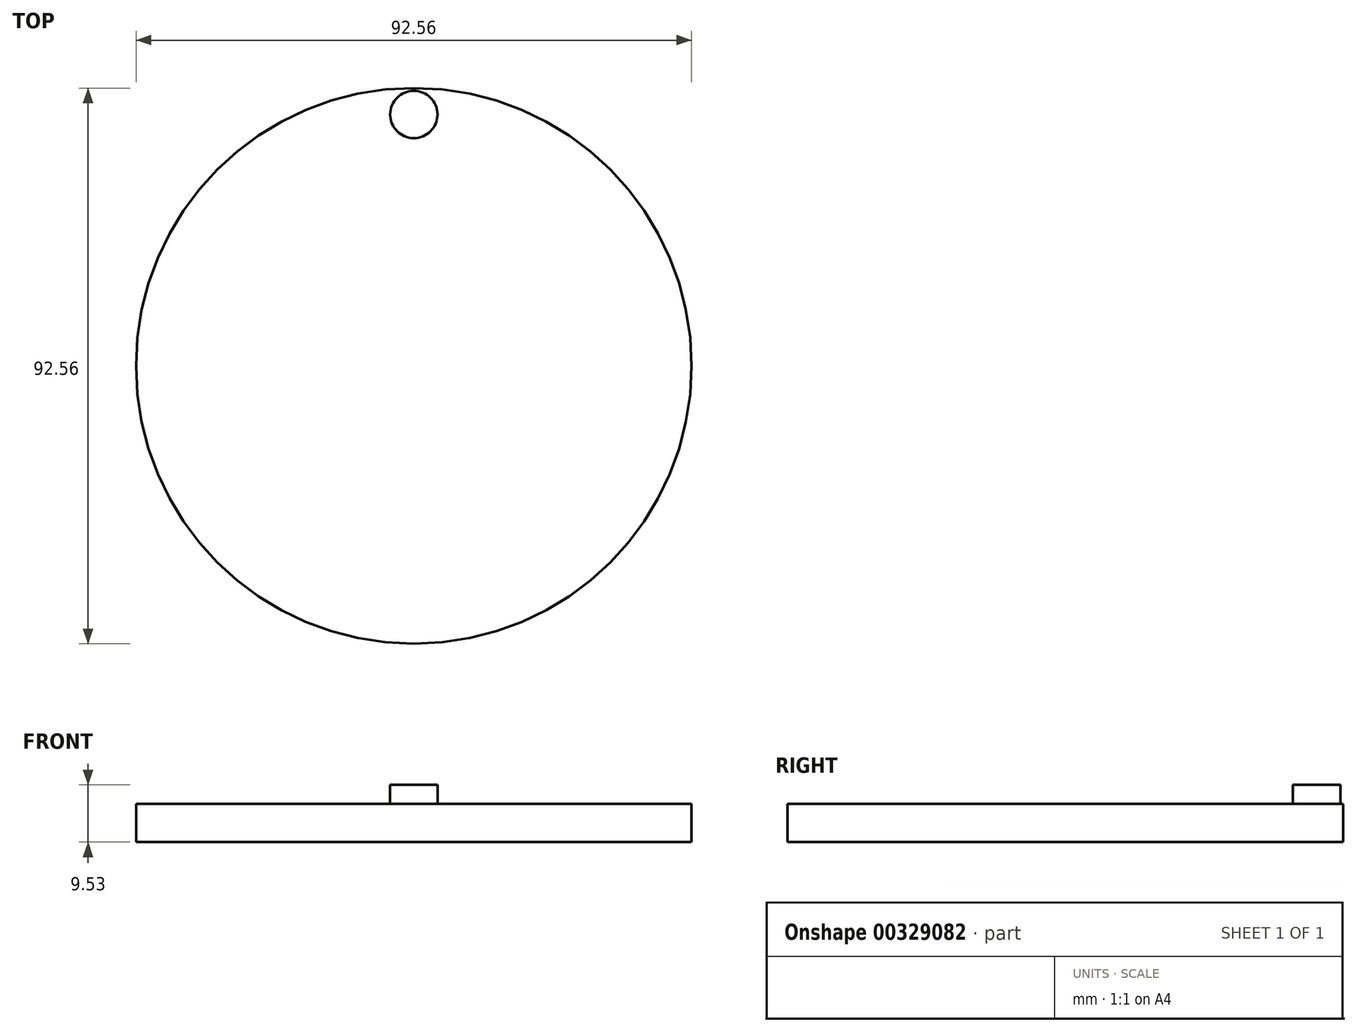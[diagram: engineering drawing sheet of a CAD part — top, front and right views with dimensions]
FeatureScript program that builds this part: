
annotation { "Feature Type Name" : "Feature", "Feature Type Description" : "" }
export const myFeature = defineFeature(function(context is Context, id is Id, definition is map)
    precondition{}
    {
        {
            var Q0;
            Q0=qCreatedBy(makeId("Top.planeOp"),FACE);
            var sketch = newSketch(context, id + "F0", { "sketchPlane" : qUnion([Q0])});
            skCircle(sketch, "E0", {"center": v(0, 0) * mm, "radius": 46.28 * mm});
            skSolve(sketch);
        }
        {
            var Q0;
            Q0=makeQuery(id+"F0.imprint","IMPRINT",FACE,{"disambiguationData":[TD([[makeQuery(id+"F0.imprint","IMPRINT",EDGE,{"derivedFrom":sQuery(id+"F0.wireOp",EDGE,"E0")}),1.0]])]});
            extrude(context, id + "F1", {"entities" : qUnion([Q0]), "depth" : 6.35 * mm, "offsetDistance" : 25.4 * mm});
        }
        {
            var Q0;
            Q0=makeQuery(id+"F1.opExtrude","CAP_FACE",FACE,{"disambiguationData":[OSD([sQuery(id+"F0.wireOp",EDGE,"E0")])],"isStart":false});
            var sketch = newSketch(context, id + "F2", { "sketchPlane" : qUnion([Q0])});
            skCircle(sketch, "E1", {"center": v(0, 41.88) * mm, "radius": 3.94 * mm});
            skSolve(sketch);
        }
        {
            var Q0;
            Q0=makeQuery(id+"F2.imprint","IMPRINT",FACE,{"disambiguationData":[TD([[makeQuery(id+"F2.imprint","IMPRINT",EDGE,{"derivedFrom":sQuery(id+"F2.wireOp",EDGE,"E1")}),1.0]])]});
            extrude(context, id + "F3", {"entities" : qUnion([Q0]), "operationType" : NewBodyOperationType.ADD, "depth" : 3.17 * mm, "offsetDistance" : 25.4 * mm});
        }
    });
